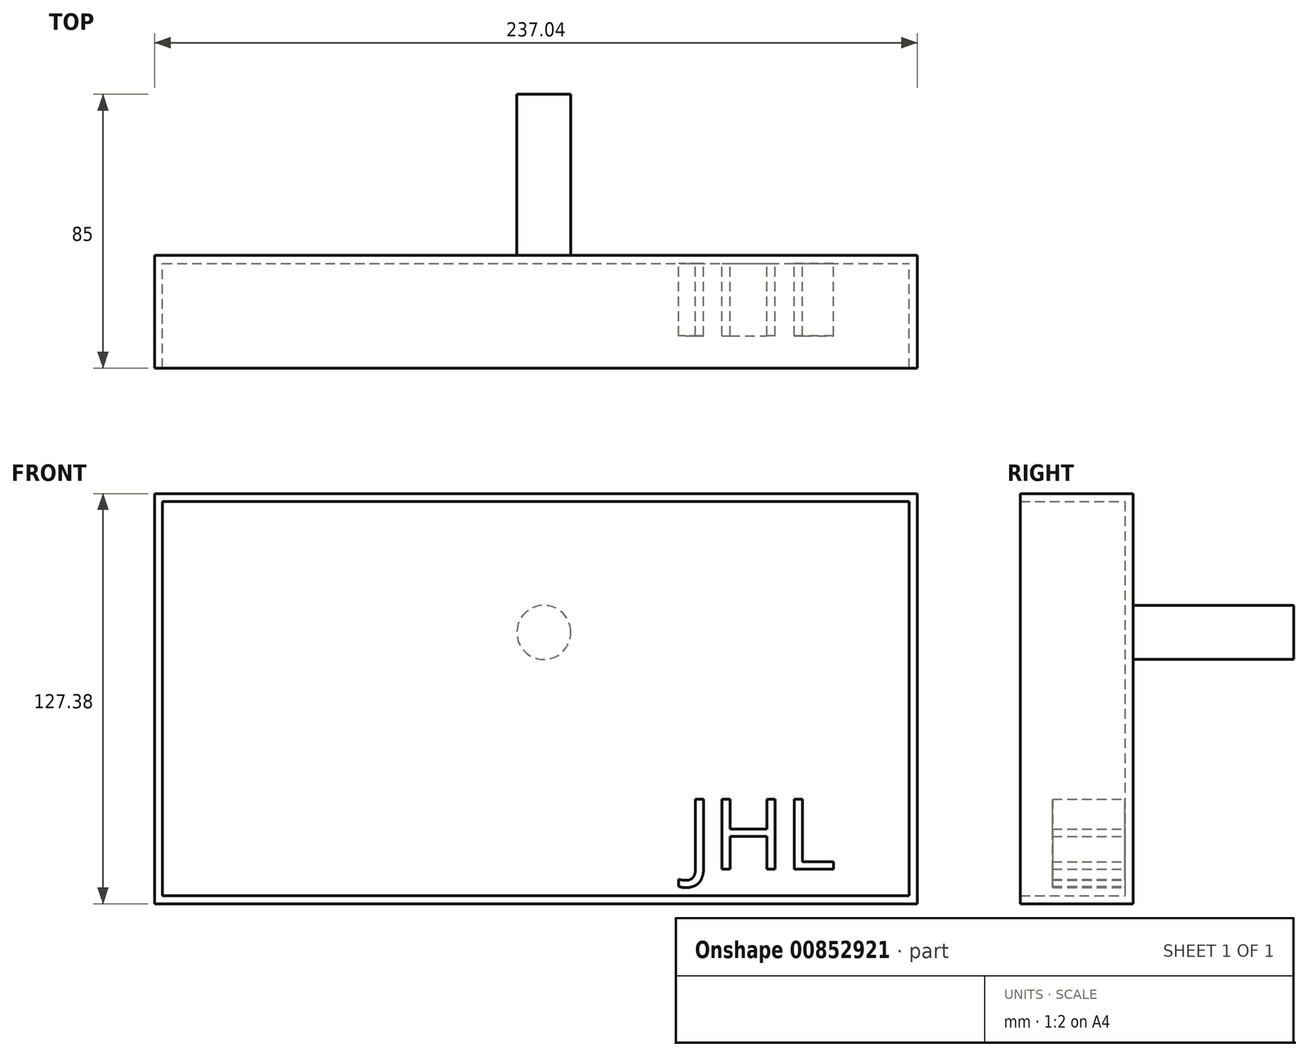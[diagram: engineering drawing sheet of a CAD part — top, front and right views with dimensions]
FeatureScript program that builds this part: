
annotation { "Feature Type Name" : "Feature", "Feature Type Description" : "" }
export const myFeature = defineFeature(function(context is Context, id is Id, definition is map)
    precondition{}
    {
        {
            var Q0;
            Q0=qCreatedBy(makeId("Front.planeOp"),FACE);
            var sketch = newSketch(context, id + "F0", { "sketchPlane" : qUnion([Q0])});
            skLineSegment(sketch, "E0.bottom", {"start": v(-120.98, 59.75) * mm, "end": v(116.06, 59.75) * mm});
            skLineSegment(sketch, "E0.top", {"start": v(-120.98, -67.63) * mm, "end": v(116.06, -67.63) * mm});
            skLineSegment(sketch, "E0.left", {"start": v(-120.98, 59.75) * mm, "end": v(-120.98, -67.63) * mm});
            skLineSegment(sketch, "E0.right", {"start": v(116.06, 59.75) * mm, "end": v(116.06, -67.63) * mm});
            skCircle(sketch, "E1", {"center": v(0, 16.64) * mm, "radius": 8.38 * mm});
            skText(sketch, "E2", { "text": "JHL", "fontName": "OpenSans-Regular.ttf"});
            const initialGuessF0  = {"E2": [0.04428, -0.0569, 1, 0, 0.02192]};
            skSetInitialGuess(sketch, initialGuessF0);
            skSolve(sketch);
        }
        {
            var Q0;
            Q0=makeQuery(id+"F0.imprint","IMPRINT",FACE,{"disambiguationData":[TD([[makeQuery(id+"F0.imprint","IMPRINT",EDGE,{"derivedFrom":sQuery(id+"F0.wireOp",EDGE,"E2.sketch_text.stroke-22")}),-1.0]])]});
            var Q1;
            Q1=makeQuery(id+"F0.imprint","IMPRINT",FACE,{"disambiguationData":[TD([[makeQuery(id+"F0.imprint","IMPRINT",EDGE,{"derivedFrom":sQuery(id+"F0.wireOp",EDGE,"E2.sketch_text.stroke-10")}),-1.0]])]});
            var Q2;
            Q2=makeQuery(id+"F0.imprint","IMPRINT",FACE,{"disambiguationData":[TD([[makeQuery(id+"F0.imprint","IMPRINT",EDGE,{"derivedFrom":sQuery(id+"F0.wireOp",EDGE,"E2.sketch_text.stroke-0")}),-1.0]])]});
            var Q3;
            Q3=makeQuery(id+"F0.imprint","IMPRINT",FACE,{"disambiguationData":[TD([[makeQuery(id+"F0.imprint","IMPRINT",EDGE,{"derivedFrom":sQuery(id+"F0.wireOp",EDGE,"E0.bottom")}),-1.0]])]});
            var Q4;
            Q4=makeQuery(id+"F0.imprint","IMPRINT",FACE,{"disambiguationData":[TD([[makeQuery(id+"F0.imprint","IMPRINT",EDGE,{"derivedFrom":sQuery(id+"F0.wireOp",EDGE,"E1")}),1.0]])]});
            extrude(context, id + "F1", {"entities" : qUnion([Q0, Q1, Q2, Q3, Q4]), "depth" : 35 * mm, "offsetDistance" : 25 * mm});
        }
        {
            var Q0;
            Q0=makeQuery(id+"F1.opExtrude","CAP_FACE",FACE,{"disambiguationData":[OSD([sQuery(id+"F0.wireOp",EDGE,"E0.bottom"),sQuery(id+"F0.wireOp",EDGE,"E0.top"),sQuery(id+"F0.wireOp",EDGE,"E0.left"),sQuery(id+"F0.wireOp",EDGE,"E0.right")])],"isStart":false});
            shell(context, id + "F2", {"entities" : qUnion([Q0]), "thickness" : 2.5 * mm});
        }
        {
            var Q0;
            Q0=makeQuery(id+"F0.imprint","IMPRINT",FACE,{"disambiguationData":[TD([[makeQuery(id+"F0.imprint","IMPRINT",EDGE,{"derivedFrom":sQuery(id+"F0.wireOp",EDGE,"E2.sketch_text.stroke-22")}),-1.0]])]});
            var Q1;
            Q1=makeQuery(id+"F0.imprint","IMPRINT",FACE,{"disambiguationData":[TD([[makeQuery(id+"F0.imprint","IMPRINT",EDGE,{"derivedFrom":sQuery(id+"F0.wireOp",EDGE,"E2.sketch_text.stroke-10")}),-1.0]])]});
            var Q2;
            Q2=makeQuery(id+"F0.imprint","IMPRINT",FACE,{"disambiguationData":[TD([[makeQuery(id+"F0.imprint","IMPRINT",EDGE,{"derivedFrom":sQuery(id+"F0.wireOp",EDGE,"E2.sketch_text.stroke-0")}),-1.0]])]});
            extrude(context, id + "F3", {"entities" : qUnion([Q0, Q1, Q2]), "operationType" : NewBodyOperationType.ADD, "depth" : 25 * mm, "offsetDistance" : 25 * mm});
        }
        {
            var Q0;
            Q0=makeQuery(id+"F0.imprint","IMPRINT",FACE,{"disambiguationData":[TD([[makeQuery(id+"F0.imprint","IMPRINT",EDGE,{"derivedFrom":sQuery(id+"F0.wireOp",EDGE,"E1")}),1.0]])]});
            extrude(context, id + "F4", {"entities" : qUnion([Q0]), "operationType" : NewBodyOperationType.ADD, "oppositeDirection" : true, "depth" : 50 * mm, "offsetDistance" : 25 * mm});
        }
    });
